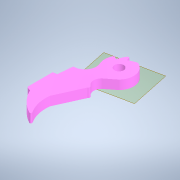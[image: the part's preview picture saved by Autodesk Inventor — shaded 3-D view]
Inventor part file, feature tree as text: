
AUTODESK INVENTOR PART (.ipt)
format: ipt  version: 2022 (Build 260153000, 153)  size: 161,792 bytes
history: native  units: mm
features: other x2, extrude x1, sketch x1
ambient origin geometry x8: Origin, YZ Plane, XZ Plane, XY Plane, X Axis, Y Axis, Z Axis, Center Point
bodies: Body1 (feature_tree)
feature tree (4):
  other  "Твердое тело1"
  other  "РабПлоскость1"
  extrude  "Выдавливание1"  Depth=5.0mm TaperAngle=0.0deg
  sketch  "Эскиз1"
